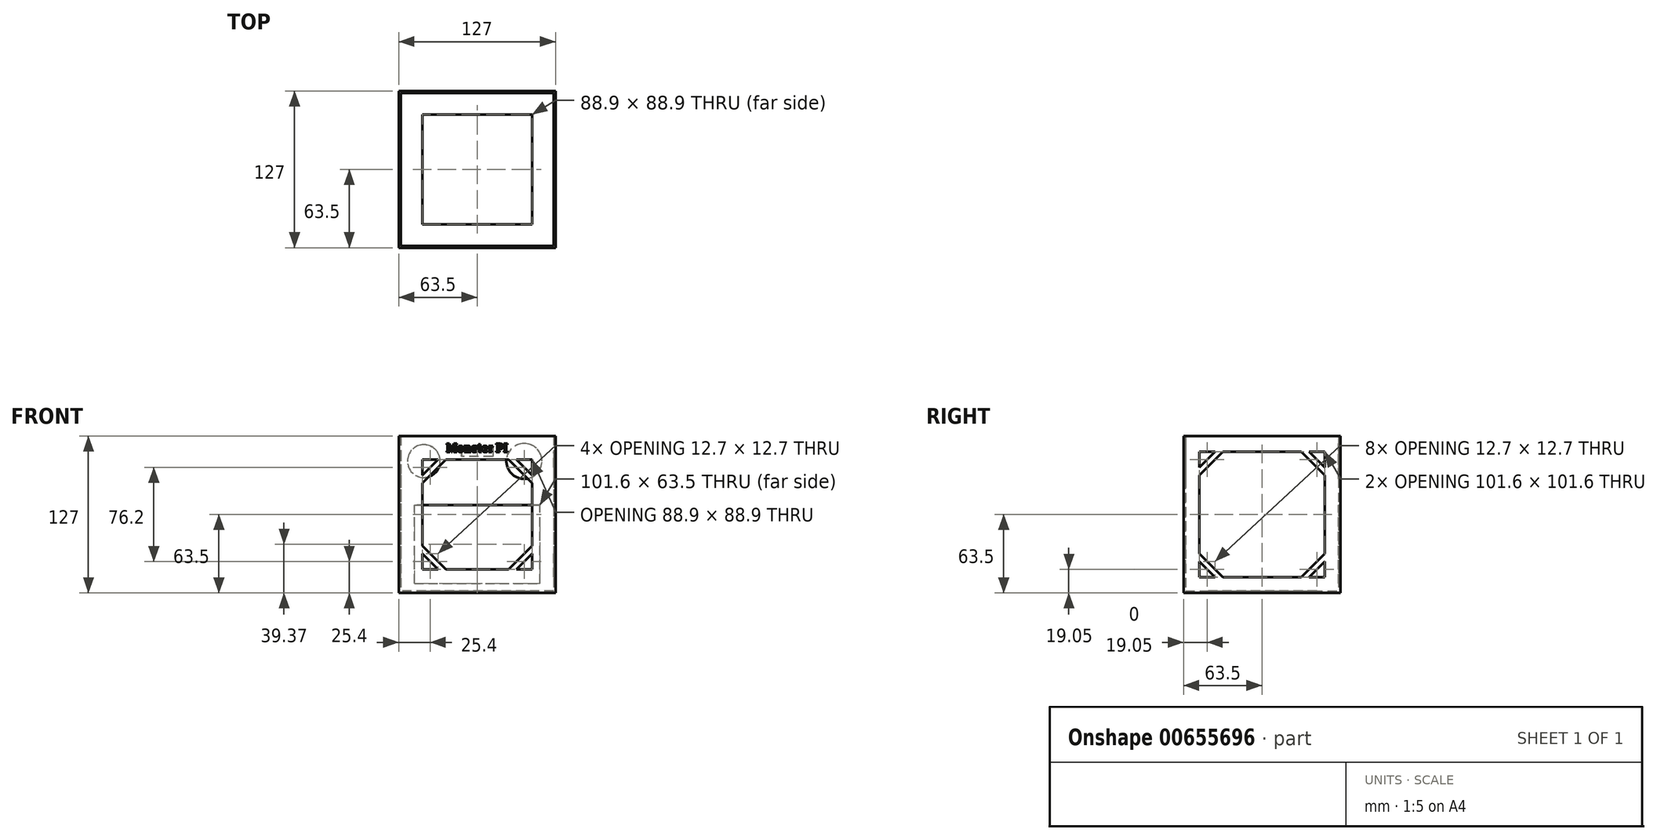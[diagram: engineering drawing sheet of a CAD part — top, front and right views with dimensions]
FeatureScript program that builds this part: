
annotation { "Feature Type Name" : "Feature", "Feature Type Description" : "" }
export const myFeature = defineFeature(function(context is Context, id is Id, definition is map)
    precondition{}
    {
        {
            var Q0;
            Q0=qCreatedBy(makeId("Front.planeOp"),FACE);
            var sketch = newSketch(context, id + "F0", { "sketchPlane" : qUnion([Q0])});
            skLineSegment(sketch, "E0.bottom", {"start": v(63.5, -63.5) * mm, "end": v(-63.5, -63.5) * mm});
            skLineSegment(sketch, "E0.top", {"start": v(63.5, 63.5) * mm, "end": v(-63.5, 63.5) * mm});
            skLineSegment(sketch, "E0.left", {"start": v(63.5, -63.5) * mm, "end": v(63.5, 63.5) * mm});
            skLineSegment(sketch, "E0.right", {"start": v(-63.5, -63.5) * mm, "end": v(-63.5, 63.5) * mm});
            skPoint(sketch, "E0.middle", {"position": v(0, 0) * mm});
            skSolve(sketch);
        }
        {
            var Q0;
            Q0 = qSketchRegion(id + "F0", true);
            extrude(context, id + "F1", {"entities" : qUnion([Q0]), "oppositeDirection" : true, "depth" : 127 * mm, "offsetDistance" : 25.4 * mm});
        }
        {
            var Q0;
            Q0=makeQuery(id+"F1.opExtrude","CAP_FACE",FACE,{"disambiguationData":[OSD([sQuery(id+"F0.wireOp",EDGE,"E0.bottom"),sQuery(id+"F0.wireOp",EDGE,"E0.top"),sQuery(id+"F0.wireOp",EDGE,"E0.left"),sQuery(id+"F0.wireOp",EDGE,"E0.right")])],"isStart":true});
            var sketch = newSketch(context, id + "F2", { "sketchPlane" : qUnion([Q0])});
            skPoint(sketch, "E1.middle", {"position": v(0, 0) * mm});
            skLineSegment(sketch, "E2", {"start": v(-44.45, 31.75) * mm, "end": v(-31.75, 44.45) * mm});
            skLineSegment(sketch, "E3", {"start": v(-44.45, 25.4) * mm, "end": v(-25.4, 44.45) * mm});
            skLineSegment(sketch, "E4", {"start": v(-44.45, 31.75) * mm, "end": v(-44.45, 44.45) * mm});
            skLineSegment(sketch, "E5", {"start": v(-44.45, 44.45) * mm, "end": v(-31.75, 44.45) * mm});
            skLineSegment(sketch, "E6", {"start": v(31.75, 44.45) * mm, "end": v(44.45, 31.75) * mm});
            skLineSegment(sketch, "E7", {"start": v(44.45, 25.4) * mm, "end": v(25.4, 44.45) * mm});
            skLineSegment(sketch, "E8", {"start": v(-44.45, -31.75) * mm, "end": v(-31.75, -44.45) * mm});
            skLineSegment(sketch, "E9", {"start": v(-44.45, -25.4) * mm, "end": v(-25.4, -44.45) * mm});
            skLineSegment(sketch, "E10", {"start": v(31.75, -44.45) * mm, "end": v(44.45, -31.75) * mm});
            skLineSegment(sketch, "E11", {"start": v(25.4, -44.45) * mm, "end": v(44.45, -25.4) * mm});
            skLineSegment(sketch, "E12", {"start": v(-25.4, 44.45) * mm, "end": v(25.4, 44.45) * mm});
            skLineSegment(sketch, "E13", {"start": v(31.75, 44.45) * mm, "end": v(44.45, 44.45) * mm});
            skLineSegment(sketch, "E14", {"start": v(44.45, 44.45) * mm, "end": v(44.45, 31.75) * mm});
            skLineSegment(sketch, "E15", {"start": v(44.45, 25.4) * mm, "end": v(44.45, -25.4) * mm});
            skLineSegment(sketch, "E16", {"start": v(44.45, -31.75) * mm, "end": v(44.45, -44.45) * mm});
            skLineSegment(sketch, "E17", {"start": v(44.45, -44.45) * mm, "end": v(31.75, -44.45) * mm});
            skLineSegment(sketch, "E18", {"start": v(25.4, -44.45) * mm, "end": v(-25.4, -44.45) * mm});
            skLineSegment(sketch, "E19", {"start": v(-31.75, -44.45) * mm, "end": v(-44.45, -44.45) * mm});
            skLineSegment(sketch, "E20", {"start": v(-44.45, -44.45) * mm, "end": v(-44.45, -31.75) * mm});
            skLineSegment(sketch, "E21", {"start": v(-44.45, -25.4) * mm, "end": v(-44.45, 25.4) * mm});
            skText(sketch, "E22", { "text": "Monster PI", "fontName": "RobotoSlab-Bold.ttf"});
            const initialGuessF2  = {"E22": [-0.02503, 0.05054, 1, 0, 0.00686]};
            skSetInitialGuess(sketch, initialGuessF2);
            skSolve(sketch);
        }
        {
            var Q0;
            Q0 = qSketchRegion(id + "F2", true);
            extrude(context, id + "F3", {"entities" : qUnion([Q0]), "operationType" : NewBodyOperationType.REMOVE, "oppositeDirection" : true, "depth" : 123.82 * mm, "offsetDistance" : 25.4 * mm});
        }
        {
            var Q0;
            Q0=makeQuery(id+"F1.opExtrude","SWEPT_FACE",FACE,{"disambiguationData":[OSD([sQuery(id+"F0.wireOp",EDGE,"E0.left")])]});
            var sketch = newSketch(context, id + "F4", { "sketchPlane" : qUnion([Q0])});
            skLineSegment(sketch, "E23", {"start": v(0, 0) * mm, "end": v(127, 0) * mm, "construction": true});
            skLineSegment(sketch, "E24", {"start": v(63.5, 63.5) * mm, "end": v(63.5, -63.5) * mm, "construction": true});
            skLineSegment(sketch, "E25.bottom", {"start": v(114.3, -50.8) * mm, "end": v(12.7, -50.8) * mm, "construction": true});
            skLineSegment(sketch, "E25.top", {"start": v(114.3, 50.8) * mm, "end": v(12.7, 50.8) * mm, "construction": true});
            skLineSegment(sketch, "E25.left", {"start": v(114.3, -50.8) * mm, "end": v(114.3, 50.8) * mm, "construction": true});
            skLineSegment(sketch, "E25.right", {"start": v(12.7, -50.8) * mm, "end": v(12.7, 50.8) * mm, "construction": true});
            skPoint(sketch, "E25.middle", {"position": v(63.5, 0) * mm});
            skLineSegment(sketch, "E26", {"start": v(12.7, 38.1) * mm, "end": v(25.4, 50.8) * mm});
            skLineSegment(sketch, "E27", {"start": v(12.7, 31.75) * mm, "end": v(31.75, 50.8) * mm});
            skLineSegment(sketch, "E28", {"start": v(101.6, 50.8) * mm, "end": v(114.3, 38.1) * mm});
            skLineSegment(sketch, "E29", {"start": v(95.25, 50.8) * mm, "end": v(114.3, 31.75) * mm});
            skLineSegment(sketch, "E30", {"start": v(12.7, -38.1) * mm, "end": v(25.4, -50.8) * mm});
            skLineSegment(sketch, "E31", {"start": v(12.7, -31.75) * mm, "end": v(31.75, -50.8) * mm});
            skLineSegment(sketch, "E32", {"start": v(101.6, -50.8) * mm, "end": v(114.3, -38.1) * mm});
            skLineSegment(sketch, "E33", {"start": v(95.25, -50.8) * mm, "end": v(114.3, -31.75) * mm});
            skLineSegment(sketch, "E34", {"start": v(12.7, -31.75) * mm, "end": v(12.7, 31.75) * mm});
            skLineSegment(sketch, "E35", {"start": v(12.7, 38.1) * mm, "end": v(12.7, 50.8) * mm});
            skLineSegment(sketch, "E36", {"start": v(25.4, 50.8) * mm, "end": v(12.7, 50.8) * mm});
            skLineSegment(sketch, "E37", {"start": v(31.75, 50.8) * mm, "end": v(95.25, 50.8) * mm});
            skLineSegment(sketch, "E38", {"start": v(101.6, 50.8) * mm, "end": v(114.3, 50.8) * mm});
            skLineSegment(sketch, "E39", {"start": v(114.3, 50.8) * mm, "end": v(114.3, 38.1) * mm});
            skLineSegment(sketch, "E40", {"start": v(114.3, 31.75) * mm, "end": v(114.3, -31.75) * mm});
            skLineSegment(sketch, "E41", {"start": v(114.3, -38.1) * mm, "end": v(114.3, -50.8) * mm});
            skLineSegment(sketch, "E42", {"start": v(114.3, -50.8) * mm, "end": v(101.6, -50.8) * mm});
            skLineSegment(sketch, "E43", {"start": v(95.25, -50.8) * mm, "end": v(31.75, -50.8) * mm});
            skLineSegment(sketch, "E44", {"start": v(25.4, -50.8) * mm, "end": v(12.7, -50.8) * mm});
            skLineSegment(sketch, "E45", {"start": v(12.7, -38.1) * mm, "end": v(12.7, -50.8) * mm});
            skSolve(sketch);
        }
        {
            var Q0;
            Q0=makeQuery(id+"F1.opExtrude","SWEPT_FACE",FACE,{"disambiguationData":[OSD([sQuery(id+"F0.wireOp",EDGE,"E0.top")])]});
            var sketch = newSketch(context, id + "F5", { "sketchPlane" : qUnion([Q0])});
            skLineSegment(sketch, "E46", {"start": v(0, 127) * mm, "end": v(0, 0) * mm, "construction": true});
            skLineSegment(sketch, "E47", {"start": v(-63.5, 63.5) * mm, "end": v(63.5, 63.5) * mm, "construction": true});
            skSolve(sketch);
        }
        {
            var Q0;
            Q0 = qSketchRegion(id + "F4", true);
            extrude(context, id + "F6", {"entities" : qUnion([Q0]), "operationType" : NewBodyOperationType.REMOVE, "endBound" : BoundingType.THROUGH_ALL, "oppositeDirection" : true, "depth" : 25.4 * mm, "offsetDistance" : 25.4 * mm});
        }
        {
            var Q0;
            Q0=qCreatedBy(makeId("Top.planeOp"),FACE);
            var sketch = newSketch(context, id + "F7", { "sketchPlane" : qUnion([Q0])});
            skLineSegment(sketch, "E48.bottom", {"start": v(61.91, 1.59) * mm, "end": v(-61.91, 1.59) * mm});
            skLineSegment(sketch, "E48.top", {"start": v(61.91, 125.41) * mm, "end": v(-61.91, 125.41) * mm});
            skLineSegment(sketch, "E48.left", {"start": v(61.91, 1.59) * mm, "end": v(61.91, 125.41) * mm});
            skLineSegment(sketch, "E48.right", {"start": v(-61.91, 1.59) * mm, "end": v(-61.91, 125.41) * mm});
            skPoint(sketch, "E48.middle", {"position": v(0, 63.5) * mm});
            skSolve(sketch);
        }
        {
            var Q0;
            Q0 = qSketchRegion(id + "F7", true);
            extrude(context, id + "F8", {"entities" : qUnion([Q0]), "operationType" : NewBodyOperationType.REMOVE, "endBound" : BoundingType.SYMMETRIC, "depth" : 123.82 * mm, "offsetDistance" : 25.4 * mm});
        }
        {
            var Q0;
            Q0=makeQuery(id+"F1.opExtrude","CAP_FACE",FACE,{"disambiguationData":[OSD([sQuery(id+"F0.wireOp",EDGE,"E0.bottom"),sQuery(id+"F0.wireOp",EDGE,"E0.top"),sQuery(id+"F0.wireOp",EDGE,"E0.left"),sQuery(id+"F0.wireOp",EDGE,"E0.right")])],"isStart":false});
            var sketch = newSketch(context, id + "F9", { "sketchPlane" : qUnion([Q0])});
            skLineSegment(sketch, "E49", {"start": v(0, 63.5) * mm, "end": v(0, -63.5) * mm, "construction": true});
            skCircle(sketch, "E50.1.0.0", {"center": v(43.18, 43.18) * mm, "radius": 13.27 * mm});
            skLineSegment(sketch, "E50.direction1", {"start": v(0, 43.18) * mm, "end": v(43.18, 43.18) * mm, "construction": true});
            skCircle(sketch, "E51", {"center": v(-38.1, 43.18) * mm, "radius": 14.35 * mm});
            skSolve(sketch);
        }
        {
            var Q0;
            Q0 = qSketchRegion(id + "F9", true);
            extrude(context, id + "F10", {"entities" : qUnion([Q0]), "operationType" : NewBodyOperationType.REMOVE, "oppositeDirection" : true, "depth" : 6.35 * mm, "offsetDistance" : 25.4 * mm});
        }
        {
            var Q0;
            Q0=makeQuery(id+"F1.opExtrude","SWEPT_FACE",FACE,{"disambiguationData":[OSD([sQuery(id+"F0.wireOp",EDGE,"E0.bottom")])]});
            var sketch = newSketch(context, id + "F11", { "sketchPlane" : qUnion([Q0])});
            skLineSegment(sketch, "E52.bottom", {"start": v(44.45, -19.05) * mm, "end": v(-44.45, -19.05) * mm});
            skLineSegment(sketch, "E52.top", {"start": v(44.45, -107.95) * mm, "end": v(-44.45, -107.95) * mm});
            skLineSegment(sketch, "E52.left", {"start": v(44.45, -19.05) * mm, "end": v(44.45, -107.95) * mm});
            skLineSegment(sketch, "E52.right", {"start": v(-44.45, -19.05) * mm, "end": v(-44.45, -107.95) * mm});
            skPoint(sketch, "E52.middle", {"position": v(0, -63.5) * mm});
            skPoint(sketch, "E52.middle.positionSnap0", {"position": v(-63.5, -63.5) * mm});
            skPoint(sketch, "E52.middle.positionSnap1", {"position": v(0, -127) * mm});
            skPoint(sketch, "E52.centerSnap0", {"position": v(-63.5, -63.5) * mm});
            skPoint(sketch, "E52.centerSnap1", {"position": v(0, -127) * mm});
            skSolve(sketch);
        }
        {
            var Q0;
            Q0 = qSketchRegion(id + "F11", true);
            extrude(context, id + "F12", {"entities" : qUnion([Q0]), "operationType" : NewBodyOperationType.REMOVE, "oppositeDirection" : true, "depth" : 25.4 * mm, "offsetDistance" : 25.4 * mm});
        }
        {
            var Q0;
            Q0=makeQuery(id+"F1.opExtrude","CAP_FACE",FACE,{"disambiguationData":[OSD([sQuery(id+"F0.wireOp",EDGE,"E0.bottom"),sQuery(id+"F0.wireOp",EDGE,"E0.top"),sQuery(id+"F0.wireOp",EDGE,"E0.left"),sQuery(id+"F0.wireOp",EDGE,"E0.right")])],"isStart":false});
            var sketch = newSketch(context, id + "F13", { "sketchPlane" : qUnion([Q0])});
            skLineSegment(sketch, "E53.bottom", {"start": v(-50.8, 7.62) * mm, "end": v(50.8, 7.62) * mm});
            skLineSegment(sketch, "E53.top", {"start": v(-50.8, -55.88) * mm, "end": v(50.8, -55.88) * mm});
            skLineSegment(sketch, "E53.left", {"start": v(-50.8, 7.62) * mm, "end": v(-50.8, -55.88) * mm});
            skLineSegment(sketch, "E53.right", {"start": v(50.8, 7.62) * mm, "end": v(50.8, -55.88) * mm});
            skPoint(sketch, "E53.middle", {"position": v(0, -24.13) * mm});
            skLineSegment(sketch, "E54.bottom", {"start": v(12.7, 46.99) * mm, "end": v(-12.7, 46.99) * mm});
            skLineSegment(sketch, "E54.top", {"start": v(12.7, 54.6) * mm, "end": v(-12.7, 54.6) * mm});
            skLineSegment(sketch, "E54.left", {"start": v(12.7, 46.99) * mm, "end": v(12.7, 54.6) * mm});
            skLineSegment(sketch, "E54.right", {"start": v(-12.7, 46.99) * mm, "end": v(-12.7, 54.6) * mm});
            skPoint(sketch, "E54.middle", {"position": v(0, 50.8) * mm});
            skPoint(sketch, "E54.middle.positionSnap0", {"position": v(0, 7.62) * mm});
            skPoint(sketch, "E54.centerSnap0", {"position": v(0, 7.62) * mm});
            skSolve(sketch);
        }
        {
            var Q0;
            Q0 = qSketchRegion(id + "F13", true);
            extrude(context, id + "F14", {"entities" : qUnion([Q0]), "operationType" : NewBodyOperationType.REMOVE, "oppositeDirection" : true, "depth" : 12.7 * mm, "offsetDistance" : 25.4 * mm});
        }
        {
            var Q0;
            {var subQ0=sQuery(id+"F0.wireOp",EDGE,"E0.top");Q0=makeQuery(id+"F5.imprint","IMPRINT",FACE,{"disambiguationData":[TD([[makeQuery(id+"F5.imprint","IMPRINT",EDGE,{"derivedFrom":makeQuery(id+"F1.opExtrude","CAP_EDGE",EDGE,{"disambiguationData":[OSD([subQ0])],"isStart":true})}),-1.0]])]});}
            var sketch = newSketch(context, id + "F15", { "sketchPlane" : qUnion([Q0])});
            skLineSegment(sketch, "E55.bottom", {"start": v(61.91, 1.59) * mm, "end": v(-61.91, 1.59) * mm});
            skLineSegment(sketch, "E55.top", {"start": v(61.91, 125.41) * mm, "end": v(-61.91, 125.41) * mm});
            skLineSegment(sketch, "E55.left", {"start": v(61.91, 1.59) * mm, "end": v(61.91, 125.41) * mm});
            skLineSegment(sketch, "E55.right", {"start": v(-61.91, 1.59) * mm, "end": v(-61.91, 125.41) * mm});
            skPoint(sketch, "E55.middle", {"position": v(0, 63.5) * mm});
            skSolve(sketch);
        }
        {
            var Q0;
            Q0 = qSketchRegion(id + "F15", true);
            extrude(context, id + "F16", {"entities" : qUnion([Q0]), "operationType" : NewBodyOperationType.REMOVE, "oppositeDirection" : true, "depth" : 1.59 * mm, "offsetDistance" : 25.4 * mm});
        }
    });
